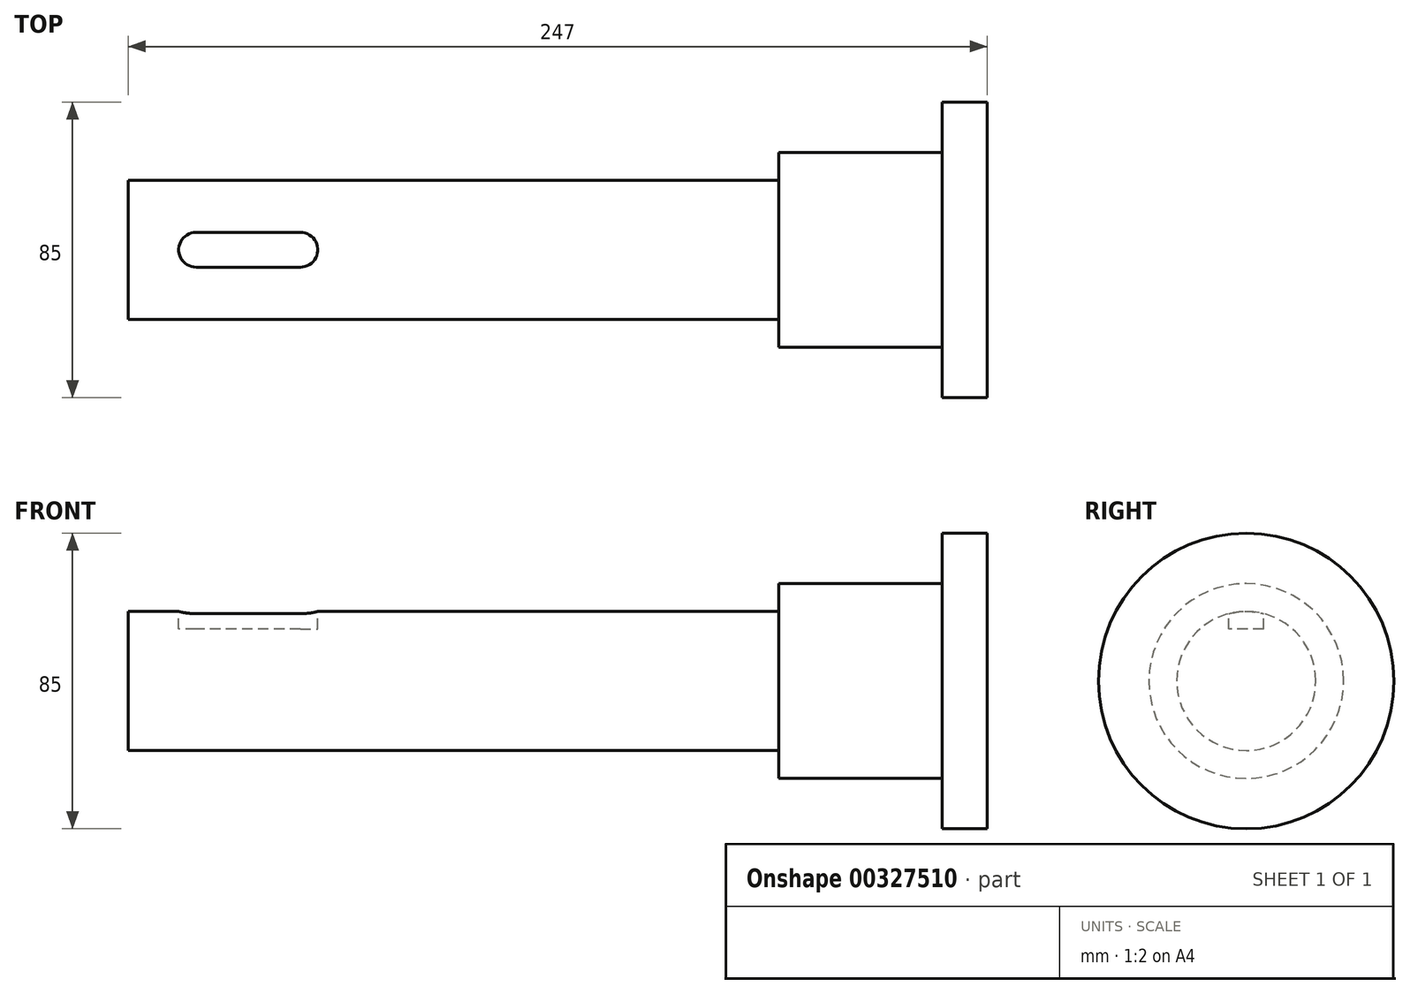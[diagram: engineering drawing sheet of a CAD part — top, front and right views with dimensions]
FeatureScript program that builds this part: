
annotation { "Feature Type Name" : "Feature", "Feature Type Description" : "" }
export const myFeature = defineFeature(function(context is Context, id is Id, definition is map)
    precondition{}
    {
        {
            var Q0;
            Q0=qCreatedBy(makeId("Front.planeOp"),FACE);
            var sketch = newSketch(context, id + "F0", { "sketchPlane" : qUnion([Q0])});
            skLineSegment(sketch, "E0.bottom", {"start": v(0, 0) * mm, "end": v(-187, 0) * mm});
            skLineSegment(sketch, "E0.top", {"start": v(0, 20) * mm, "end": v(-187, 20) * mm});
            skLineSegment(sketch, "E0.left", {"start": v(0, 0) * mm, "end": v(0, 20) * mm});
            skLineSegment(sketch, "E0.right", {"start": v(-187, 0) * mm, "end": v(-187, 20) * mm});
            skLineSegment(sketch, "E1.bottom", {"start": v(0, 0) * mm, "end": v(47, 0) * mm});
            skLineSegment(sketch, "E1.top", {"start": v(0, 28) * mm, "end": v(47, 28) * mm});
            skLineSegment(sketch, "E1.left", {"start": v(0, 0) * mm, "end": v(0, 28) * mm});
            skLineSegment(sketch, "E1.right", {"start": v(47, 0) * mm, "end": v(47, 28) * mm});
            skLineSegment(sketch, "E2.bottom", {"start": v(47, 0) * mm, "end": v(60, 0) * mm});
            skLineSegment(sketch, "E2.top", {"start": v(47, 42.5) * mm, "end": v(60, 42.5) * mm});
            skLineSegment(sketch, "E2.left", {"start": v(47, 0) * mm, "end": v(47, 42.5) * mm});
            skLineSegment(sketch, "E2.right", {"start": v(60, 0) * mm, "end": v(60, 42.5) * mm});
            skLineSegment(sketch, "E3", {"start": v(133.9, 0) * mm, "end": v(-297.9, 0) * mm});
            skSolve(sketch);
        }
        {
            var Q0;
            {var subQ3=sQuery(id+"F0.wireOp",EDGE,"E2.top");Q0=makeQuery(id+"F0.imprint","IMPRINT",FACE,{"disambiguationData":[TD([[makeQuery(id+"F0.imprint","IMPRINT",EDGE,{"derivedFrom":subQ3}),-1.0]])]});}
            var Q1;
            {var subQ0=sQuery(id+"F0.wireOp",EDGE,"E0.top");Q1=makeQuery(id+"F0.imprint","IMPRINT",FACE,{"disambiguationData":[TD([[makeQuery(id+"F0.imprint","IMPRINT",EDGE,{"derivedFrom":subQ0}),1.0]])]});}
            var Q2;
            {var subQ1=sQuery(id+"F0.wireOp",EDGE,"E1.top");Q2=makeQuery(id+"F0.imprint","IMPRINT",FACE,{"disambiguationData":[TD([[makeQuery(id+"F0.imprint","IMPRINT",EDGE,{"derivedFrom":subQ1}),-1.0]])]});}
            var Q3;
            Q3=sQuery(id+"F0.wireOp",EDGE,"E3");
            revolve(context, id + "F1", {"entities" : qUnion([Q0, Q1, Q2]), "axis" : qUnion([Q3]), "revolveType" : RevolveType.FULL});
        }
        {
            var Q0;
            Q0=qCreatedBy(makeId("Top.planeOp"),FACE);
            var sketch = newSketch(context, id + "F2", { "sketchPlane" : qUnion([Q0])});
            skLineSegment(sketch, "E4", {"start": v(-187, 20) * mm, "end": v(0, 20) * mm});
            skLineSegment(sketch, "E5.0", {"start": v(-187, 20) * mm, "end": v(-187, -20) * mm});
            skLineSegment(sketch, "E6", {"start": v(0, -20) * mm, "end": v(-187, -20) * mm});
            skLineSegment(sketch, "E7", {"start": v(47, -28) * mm, "end": v(0, -28) * mm});
            skLineSegment(sketch, "E8", {"start": v(0, 28) * mm, "end": v(47, 28) * mm});
            skLineSegment(sketch, "E9.0", {"start": v(47, 42.5) * mm, "end": v(47, -42.5) * mm});
            skLineSegment(sketch, "E10", {"start": v(47, 42.5) * mm, "end": v(60, 42.5) * mm});
            skLineSegment(sketch, "E11", {"start": v(60, -42.5) * mm, "end": v(47, -42.5) * mm});
            skLineSegment(sketch, "E12", {"start": v(-187, 0) * mm, "end": v(-167.5, 0) * mm});
            skCircle(sketch, "E13", {"center": v(-167.5, 0) * mm, "radius": 5 * mm});
            skLineSegment(sketch, "E14", {"start": v(-167.5, 0) * mm, "end": v(-137.5, 0) * mm});
            skCircle(sketch, "E15", {"center": v(-137.5, 0) * mm, "radius": 5 * mm});
            skLineSegment(sketch, "E16", {"start": v(-137.5, 0) * mm, "end": v(-137.5, 5) * mm});
            skLineSegment(sketch, "E17", {"start": v(-137.5, 5) * mm, "end": v(-167.5, 5) * mm});
            skLineSegment(sketch, "E18", {"start": v(-137.5, 0) * mm, "end": v(-137.5, -5) * mm});
            skLineSegment(sketch, "E19", {"start": v(-137.5, -5) * mm, "end": v(-167.5, -5) * mm});
            skSolve(sketch);
        }
        {
            var Q0;
            Q0 = qSketchRegion(id + "F2", true);
            extrude(context, id + "F3", {"entities" : qUnion([Q0]), "operationType" : NewBodyOperationType.ADD, "depth" : 100 * mm});
        }
        {
            var Q0;
            Q0=makeQuery(id+"F3.opExtrude","CAP_FACE",FACE,{"disambiguationData":[OSD([sQuery(id+"F2.wireOp",EDGE,"E13"),sQuery(id+"F2.wireOp",EDGE,"E15"),sQuery(id+"F2.wireOp",EDGE,"E17"),sQuery(id+"F2.wireOp",EDGE,"E19")])],"isStart":false});
            extrude(context, id + "F4", {"entities" : qUnion([Q0]), "operationType" : NewBodyOperationType.REMOVE, "oppositeDirection" : true, "depth" : 85 * mm});
        }
    });
